# Revit family: 304_94118dd5f4e4458cb6905cf8afe554
name_source: partatom
category: Pipe Accessories
units: mm (PartAtom-declared; Revit-internal decimal feet)

## family parameters
Always vertical = Yes
Cut with Voids When Loaded = No
Part Type = Valve - Breaks Into
Round Connector Dimension = Use Diameter
Shared = No
Work Plane-Based = No

## types (3) — shared parameters
Description = PI zone valve, Internal thread
H1 = 10 mm  [stored 0.0328084 ft]
H1__ve = -10 mm  [stored -0.0328084 ft]
H2 = 4 mm  [stored 0.0131234 ft]
H2__ve = -4 mm  [stored -0.0131234 ft]
H3 = 3 mm  [stored 0.00984252 ft]
L1 = 14 mm  [stored 0.0459318 ft]
L1__ve = -14 mm  [stored -0.0459318 ft]
L2 = 15 mm  [stored 0.0492126 ft]
L2D = 96 mm  [stored 0.314961 ft]
L2D_Min = 3048 mm  [stored 10 ft]
Manufacturer = Belimo
QmdConnectorList = 301;D;302;D
R2 = 6 mm  [stored 0.019685 ft]
R3 = 4 mm  [stored 0.0131234 ft]
W2D = 15 mm  [stored 0.0492126 ft]
magiPartTypeId = 304
magiProductFamilyId = 94118dd5f4e4458cb6905cf8afe554

## per-type parameters (varying)
| type | CenSd_R_6 | D | H | L3 | LL | R | R1 | magiProductId |
| C215QP-B | 13 mm | 15 mm | 26 mm  [stored 0.0853018 ft] | 38 mm  [stored 0.124672 ft] | 48 mm  [stored 0.15748 ft] | 15 mm  [stored 0.0492126 ft] | 26 mm  [stored 0.0853018 ft] | 660a0752628d43778be596e12ee1e4 |
| C215QP-D | 13 mm | 15 mm | 26 mm  [stored 0.0853018 ft] | 38 mm  [stored 0.124672 ft] | 48 mm  [stored 0.15748 ft] | 15 mm  [stored 0.0492126 ft] | 26 mm  [stored 0.0853018 ft] | 403501f185054812a94336e6ee676c |
| C220QP-F | 15 mm  [stored 0.0492126 ft] | 20 mm | 31 mm  [stored 0.101706 ft] | 48 mm  [stored 0.15748 ft] | 53 mm  [stored 0.173885 ft] | 17 mm  [stored 0.0557743 ft] | 32 mm | cac872b7608a49d1b07e5de468ac6f |

note: column(s) folded — value = type name in every type: MC Product Code

note: [stored X ft] marks values corroborated as IEEE doubles in the binary element streams (Revit-internal decimal feet)

## geometry (parser evidence)
native form markers: Blend x2, Sweep x3
no freeform markers — native parametric forms only
